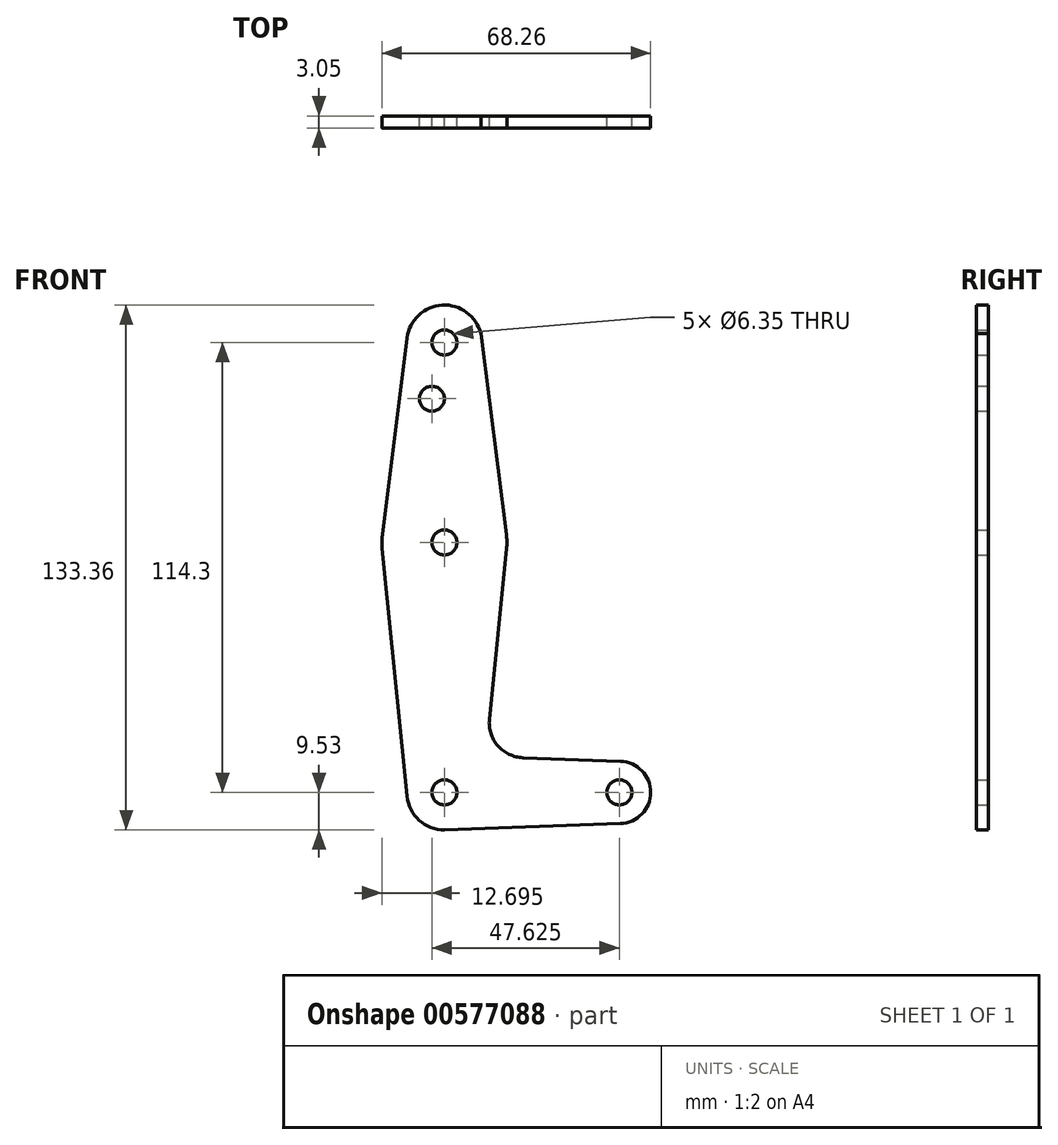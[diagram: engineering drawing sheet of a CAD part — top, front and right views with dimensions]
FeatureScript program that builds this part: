
annotation { "Feature Type Name" : "Feature", "Feature Type Description" : "" }
export const myFeature = defineFeature(function(context is Context, id is Id, definition is map)
    precondition{}
    {
        {
            var Q0;
            Q0=qCreatedBy(makeId("Front.planeOp"),FACE);
            var sketch = newSketch(context, id + "F0", { "sketchPlane" : qUnion([Q0])});
            skLineSegment(sketch, "E0", {"start": v(0, 0) * mm, "end": v(0, 114.3) * mm, "construction": true});
            skLineSegment(sketch, "E1", {"start": v(0, 0) * mm, "end": v(44.45, 0) * mm, "construction": true});
            skArc(sketch, "E2", {"start": v(-9.48, -0.95) * mm, "mid": v(-6.13, -7.29) * mm, "end": v(0.68, -9.5) * mm});
            skArc(sketch, "E3", {"start": v(9.52, 114.41) * mm, "mid": v(0.54, 123.8) * mm, "end": v(-9.45, 115.5) * mm});
            skArc(sketch, "E4", {"start": v(44.73, -7.93) * mm, "mid": v(52.39, 0) * mm, "end": v(44.73, 7.93) * mm});
            skArc(sketch, "E5", {"start": v(-15.75, 65.48) * mm, "mid": v(-15.87, 63.7) * mm, "end": v(-15.8, 61.91) * mm});
            skPoint(sketch, "E6.startSnap0", {"position": v(22.22, 0) * mm});
            skCircle(sketch, "E7", {"center": v(-3.18, 100.01) * mm, "radius": 3.18 * mm});
            skCircle(sketch, "E8", {"center": v(0, 114.3) * mm, "radius": 3.18 * mm});
            skCircle(sketch, "E9", {"center": v(0, 63.5) * mm, "radius": 3.18 * mm});
            skCircle(sketch, "E10", {"center": v(0, 0) * mm, "radius": 3.18 * mm});
            skCircle(sketch, "E11", {"center": v(44.45, 0) * mm, "radius": 3.18 * mm});
            skLineSegment(sketch, "E12", {"start": v(-9.45, 115.5) * mm, "end": v(-15.75, 65.48) * mm});
            skLineSegment(sketch, "E13", {"start": v(9.25, 116.57) * mm, "end": v(15.75, 65.5) * mm});
            skLineSegment(sketch, "E14", {"start": v(-9.48, -0.95) * mm, "end": v(-15.8, 61.91) * mm});
            skLineSegment(sketch, "E15", {"start": v(11.44, 18.6) * mm, "end": v(15.8, 61.91) * mm});
            skLineSegment(sketch, "E16", {"start": v(19.97, 8.82) * mm, "end": v(44.73, 7.93) * mm});
            skLineSegment(sketch, "E17", {"start": v(0, -9.52) * mm, "end": v(44.73, -7.93) * mm});
            skArc(sketch, "E18.filletArc", {"start": v(11.44, 18.6) * mm, "mid": v(13.59, 11.86) * mm, "end": v(19.97, 8.82) * mm});
            skArc(sketch, "E19.trimOffspring", {"start": v(15.8, 61.91) * mm, "mid": v(15.87, 63.7) * mm, "end": v(15.75, 65.5) * mm});
            skSolve(sketch);
        }
        {
            var Q0;
            {var subQ8=sQuery(id+"F0.wireOp",EDGE,"E4");Q0=makeQuery(id+"F0.imprint","IMPRINT",FACE,{"disambiguationData":[TD([[makeQuery(id+"F0.imprint","IMPRINT",EDGE,{"derivedFrom":subQ8}),1.0]])]});}
            extrude(context, id + "F1", {"entities" : qUnion([Q0]), "depth" : 3.05 * mm, "offsetDistance" : 25.4 * mm});
        }
    });
